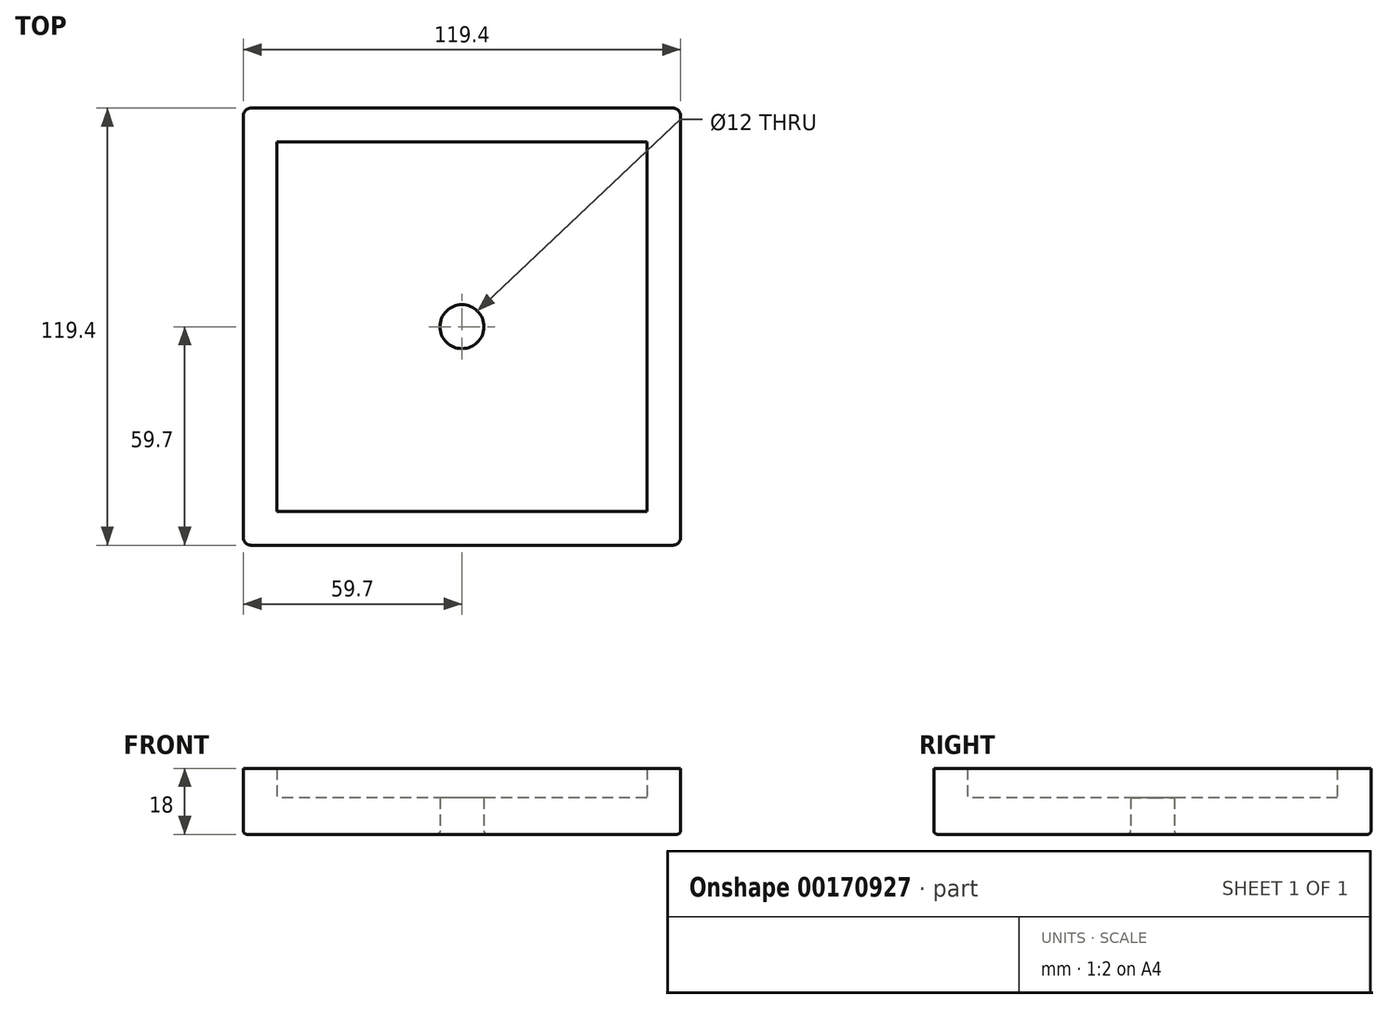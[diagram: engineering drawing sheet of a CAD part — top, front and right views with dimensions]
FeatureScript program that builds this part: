
annotation { "Feature Type Name" : "Feature", "Feature Type Description" : "" }
export const myFeature = defineFeature(function(context is Context, id is Id, definition is map)
    precondition{}
    {
        {
            var Q0;
            Q0=qCreatedBy(makeId("Top.planeOp"),FACE);
            var sketch = newSketch(context, id + "F0", { "sketchPlane" : qUnion([Q0])});
            skLineSegment(sketch, "E0.bottom", {"start": v(50.5, 50.5) * mm, "end": v(-50.5, 50.5) * mm});
            skLineSegment(sketch, "E0.top", {"start": v(50.5, -50.5) * mm, "end": v(-50.5, -50.5) * mm});
            skLineSegment(sketch, "E0.left", {"start": v(50.5, 50.5) * mm, "end": v(50.5, -50.5) * mm});
            skLineSegment(sketch, "E0.right", {"start": v(-50.5, 50.5) * mm, "end": v(-50.5, -50.5) * mm});
            skPoint(sketch, "E0.middle", {"position": v(0, 0) * mm});
            skLineSegment(sketch, "E1.bottom", {"start": v(59.7, 59.7) * mm, "end": v(-59.7, 59.7) * mm});
            skLineSegment(sketch, "E1.top", {"start": v(59.7, -59.7) * mm, "end": v(-59.7, -59.7) * mm});
            skLineSegment(sketch, "E1.left", {"start": v(59.7, 59.7) * mm, "end": v(59.7, -59.7) * mm});
            skLineSegment(sketch, "E1.right", {"start": v(-59.7, 59.7) * mm, "end": v(-59.7, -59.7) * mm});
            skCircle(sketch, "E2", {"center": v(0, 0) * mm, "radius": 6 * mm});
            skSolve(sketch);
        }
        {
            var Q0;
            Q0=makeQuery(id+"F0.imprint","IMPRINT",FACE,{"disambiguationData":[TD([[makeQuery(id+"F0.imprint","IMPRINT",EDGE,{"derivedFrom":sQuery(id+"F0.wireOp",EDGE,"E0.bottom")}),1.0]])]});
            extrude(context, id + "F1", {"entities" : qUnion([Q0]), "depth" : 10 * mm});
        }
        {
            var Q0;
            Q0=makeQuery(id+"F0.imprint","IMPRINT",FACE,{"disambiguationData":[TD([[makeQuery(id+"F0.imprint","IMPRINT",EDGE,{"derivedFrom":sQuery(id+"F0.wireOp",EDGE,"E0.bottom")}),-1.0]])]});
            extrude(context, id + "F2", {"entities" : qUnion([Q0]), "operationType" : NewBodyOperationType.ADD, "depth" : 18 * mm});
        }
        {
            var Q0;
            Q0=makeQuery(id+"F2.opExtrude","SWEPT_EDGE",EDGE,{"disambiguationData":[OSD([sQuery(id+"F0.wireOp",EDGE,"E1.top"),sQuery(id+"F0.wireOp",EDGE,"E1.right")])]});
            var Q1;
            Q1=makeQuery(id+"F2.opExtrude","SWEPT_EDGE",EDGE,{"disambiguationData":[OSD([sQuery(id+"F0.wireOp",EDGE,"E1.top"),sQuery(id+"F0.wireOp",EDGE,"E1.left")])]});
            var Q2;
            Q2=makeQuery(id+"F2.opExtrude","SWEPT_EDGE",EDGE,{"disambiguationData":[OSD([sQuery(id+"F0.wireOp",EDGE,"E1.bottom"),sQuery(id+"F0.wireOp",EDGE,"E1.left")])]});
            var Q3;
            Q3=makeQuery(id+"F2.opExtrude","SWEPT_EDGE",EDGE,{"disambiguationData":[OSD([sQuery(id+"F0.wireOp",EDGE,"E1.bottom"),sQuery(id+"F0.wireOp",EDGE,"E1.right")])]});
            fillet(context, id + "F3", {"entities" : qUnion([Q0, Q1, Q2, Q3]), "radius" : 2 * mm, "tangentPropagation" : true, "allowEdgeOverflow" : false});
        }
        {
            var Q0;
            {var subQ0=sQuery(id+"F0.wireOp",EDGE,"E0.right");var subQ1=sQuery(id+"F0.wireOp",EDGE,"E0.left");var subQ2=sQuery(id+"F0.wireOp",EDGE,"E0.top");var subQ3=sQuery(id+"F0.wireOp",EDGE,"E0.bottom");Q0=makeQuery(id+"F2.boolean.opBoolean","MERGE",FACE,{"derivedFrom":[makeQuery(id+"F1.opExtrude","CAP_FACE",FACE,{"disambiguationData":[OSD([subQ3,subQ2,subQ1,subQ0,sQuery(id+"F0.wireOp",EDGE,"E2")])],"isStart":true}),makeQuery(id+"F2.opExtrude","CAP_FACE",FACE,{"disambiguationData":[OSD([subQ3,subQ2,subQ1,subQ0,sQuery(id+"F0.wireOp",EDGE,"E1.bottom"),sQuery(id+"F0.wireOp",EDGE,"E1.top"),sQuery(id+"F0.wireOp",EDGE,"E1.left"),sQuery(id+"F0.wireOp",EDGE,"E1.right")])],"isStart":true})]});}
            fillet(context, id + "F4", {"entities" : qUnion([Q0]), "radius" : 1 * mm, "tangentPropagation" : true, "allowEdgeOverflow" : false});
        }
    });
